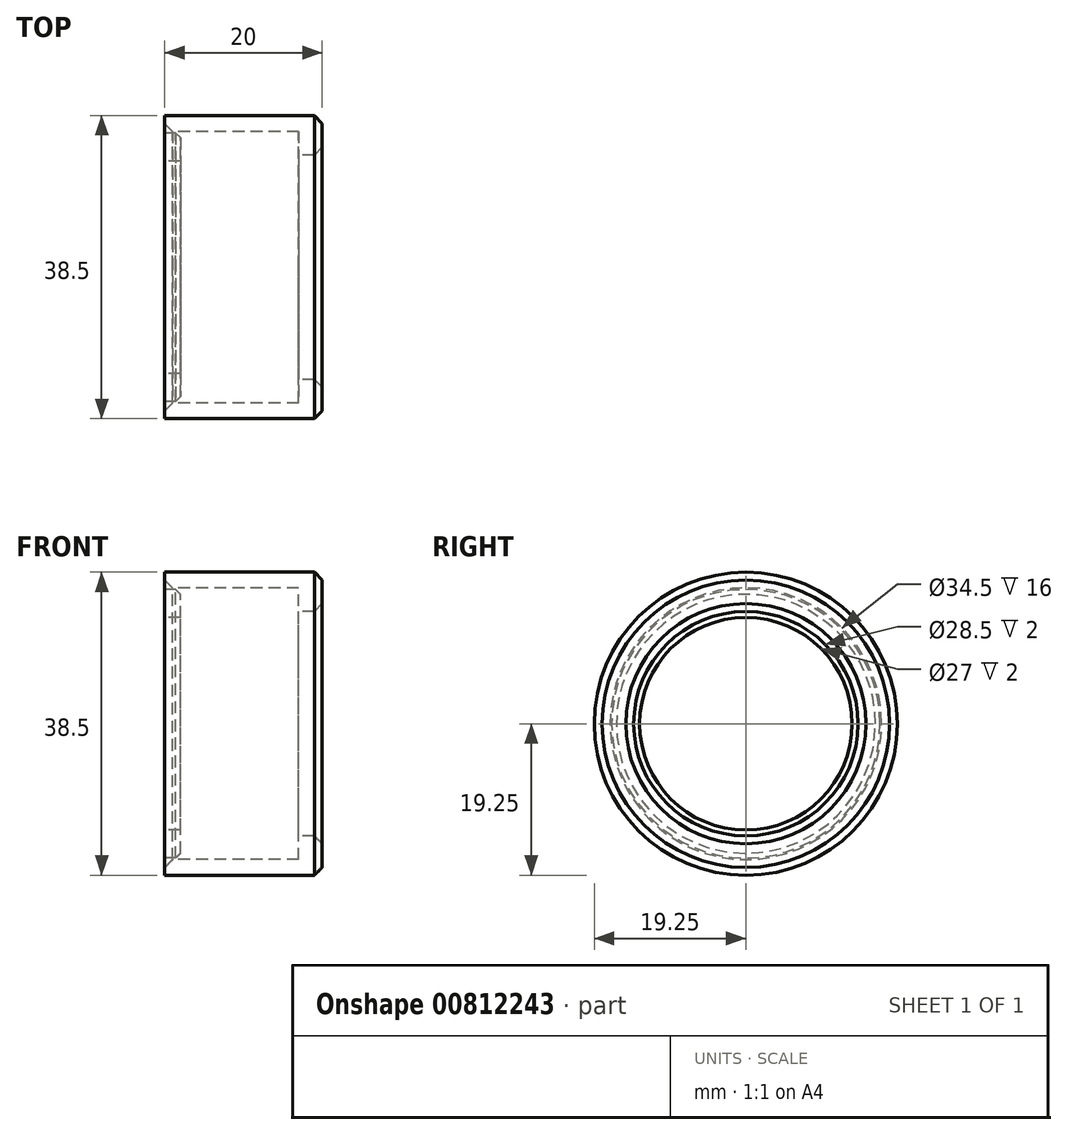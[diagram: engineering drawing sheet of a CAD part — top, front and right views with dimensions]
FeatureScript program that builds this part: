
annotation { "Feature Type Name" : "Feature", "Feature Type Description" : "" }
export const myFeature = defineFeature(function(context is Context, id is Id, definition is map)
    precondition{}
    {
        {
            var Q0;
            Q0=qCreatedBy(makeId("Right.planeOp"),FACE);
            var sketch = newSketch(context, id + "F0", { "sketchPlane" : qUnion([Q0])});
            skCircle(sketch, "E0", {"center": v(0, 0) * mm, "radius": 17.05 * mm, "construction": true});
            skCircle(sketch, "E1.0", {"center": v(0, 0) * mm, "radius": 17.25 * mm});
            skCircle(sketch, "E2.0", {"center": v(0, 0) * mm, "radius": 19.25 * mm});
            skSolve(sketch);
        }
        {
            var Q0;
            Q0 = qSketchRegion(id + "F0", true);
            extrude(context, id + "F1", {"entities" : qUnion([Q0]), "depth" : 17 * mm, "offsetDistance" : 25 * mm});
        }
        {
            var Q0;
            Q0=makeQuery(id+"F1.opExtrude","CAP_FACE",FACE,{"disambiguationData":[OSD([sQuery(id+"F0.wireOp",EDGE,"E1.0"),sQuery(id+"F0.wireOp",EDGE,"E2.0")])],"isStart":false});
            var sketch = newSketch(context, id + "F2", { "sketchPlane" : qUnion([Q0])});
            skCircle(sketch, "E3.0", {"center": v(0, 0) * mm, "radius": 19.25 * mm});
            skCircle(sketch, "E4.0", {"center": v(0, 0) * mm, "radius": 17.25 * mm, "construction": true});
            skCircle(sketch, "E5.0", {"center": v(0, 0) * mm, "radius": 14.25 * mm});
            skSolve(sketch);
        }
        {
            var Q0;
            Q0 = qSketchRegion(id + "F2", true);
            extrude(context, id + "F3", {"entities" : qUnion([Q0]), "operationType" : NewBodyOperationType.ADD, "depth" : 3 * mm, "offsetDistance" : 25 * mm});
        }
        {
            var Q0;
            Q0=makeQuery(id+"F3.opExtrude","CAP_EDGE",EDGE,{"disambiguationData":[OSD([sQuery(id+"F2.wireOp",EDGE,"E3.0")])],"isStart":false});
            var Q1;
            Q1=makeQuery(id+"F3.opExtrude","CAP_EDGE",EDGE,{"disambiguationData":[OSD([sQuery(id+"F2.wireOp",EDGE,"E5.0")])],"isStart":false});
            var Q2;
            Q2=makeQuery(id+"F1.opExtrude","CAP_EDGE",EDGE,{"disambiguationData":[OSD([sQuery(id+"F0.wireOp",EDGE,"E1.0")])],"isStart":true});
            chamfer(context, id + "F4", {"entities" : qUnion([Q0, Q1, Q2]), "width" : 1 * mm, "tangentPropagation" : true});
        }
        {
            var Q0;
            Q0=qCreatedBy(makeId("Right.planeOp"),FACE);
            var sketch = newSketch(context, id + "F5", { "sketchPlane" : qUnion([Q0])});
            skCircle(sketch, "E6", {"center": v(0, 0) * mm, "radius": 13.5 * mm});
            skCircle(sketch, "E7", {"center": v(0, 0) * mm, "radius": 17.05 * mm});
            skSolve(sketch);
        }
        {
            var Q0;
            Q0 = qSketchRegion(id + "F5", true);
            extrude(context, id + "F6", {"entities" : qUnion([Q0]), "depth" : 2 * mm, "offsetDistance" : 25 * mm});
        }
        {
            var Q0;
            Q0=makeQuery(id+"F6.opExtrude","CAP_EDGE",EDGE,{"disambiguationData":[OSD([sQuery(id+"F5.wireOp",EDGE,"E7")])],"isStart":false});
            chamfer(context, id + "F7", {"entities" : qUnion([Q0]), "width" : .6 * mm, "tangentPropagation" : true});
        }
    });
